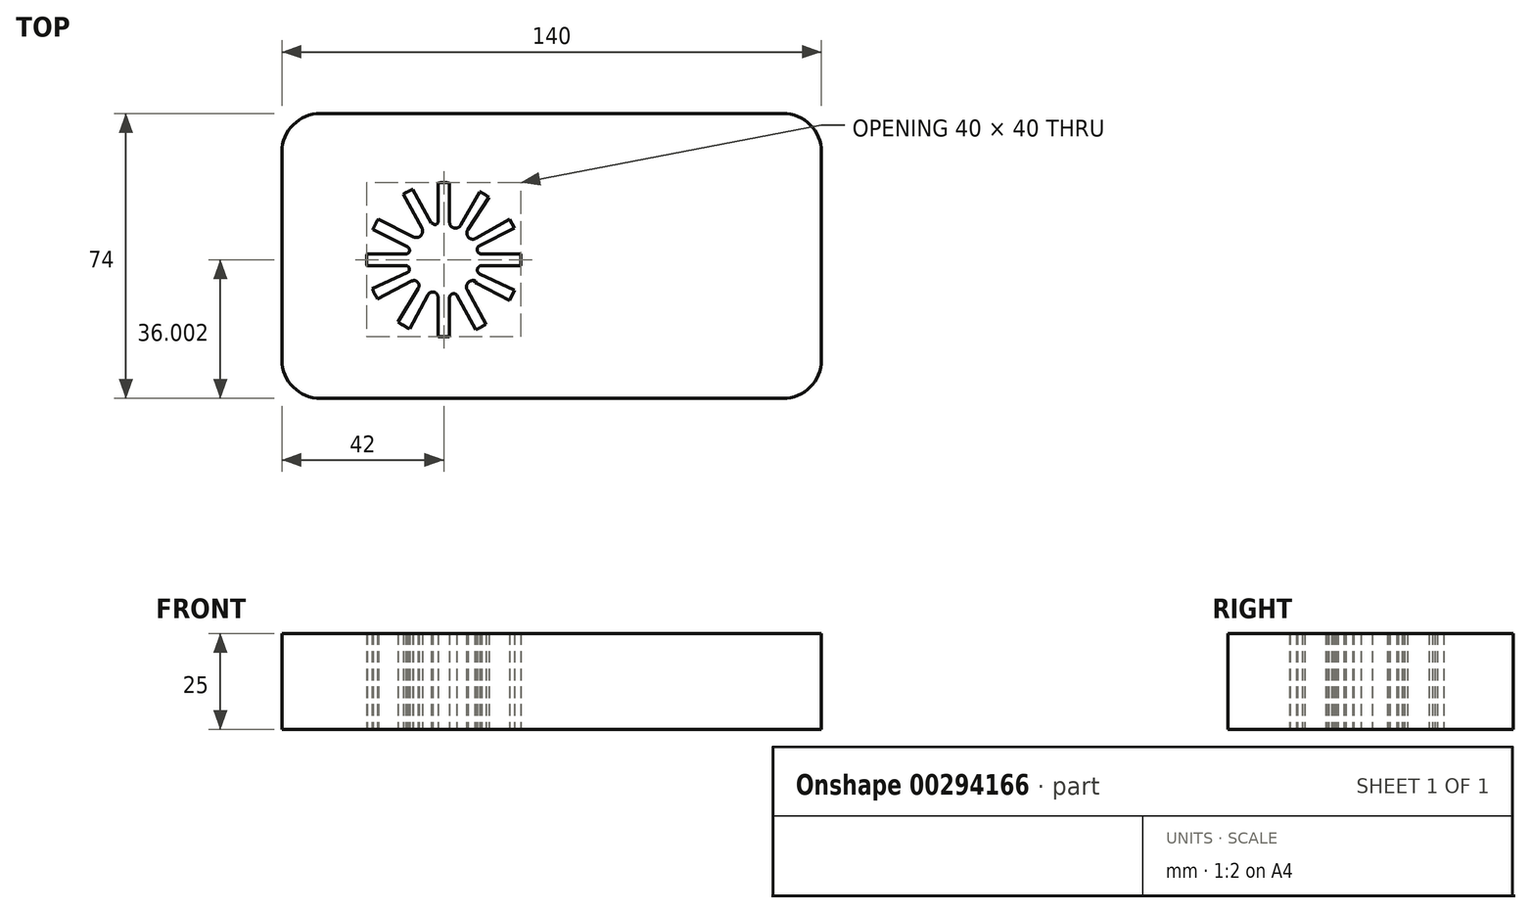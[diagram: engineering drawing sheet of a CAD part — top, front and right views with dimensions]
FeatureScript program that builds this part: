
annotation { "Feature Type Name" : "Feature", "Feature Type Description" : "" }
export const myFeature = defineFeature(function(context is Context, id is Id, definition is map)
    precondition{}
    {
        {
            var Q0;
            Q0=qCreatedBy(makeId("Top.planeOp"),FACE);
            var sketch = newSketch(context, id + "F0", { "sketchPlane" : qUnion([Q0])});
            skArc(sketch, "E0", {"start": v(-58.42, 28.76) * mm, "mid": v(-58.53, 27.26) * mm, "end": v(-58.42, 25.76) * mm});
            skLineSegment(sketch, "E1", {"start": v(-68.47, 28.76) * mm, "end": v(-58.42, 28.76) * mm});
            skLineSegment(sketch, "E2", {"start": v(-68.47, 25.76) * mm, "end": v(-58.42, 25.76) * mm});
            skLineSegment(sketch, "E3", {"start": v(-50.03, 17.38) * mm, "end": v(-50.03, 7.32) * mm});
            skLineSegment(sketch, "E4", {"start": v(-50.03, 7.32) * mm, "end": v(-50.03, 17.38) * mm});
            skLineSegment(sketch, "E5", {"start": v(-47.03, 17.38) * mm, "end": v(-47.03, 7.32) * mm});
            skLineSegment(sketch, "E6", {"start": v(-38.64, 25.76) * mm, "end": v(-28.59, 25.76) * mm});
            skLineSegment(sketch, "E7", {"start": v(-28.59, 25.76) * mm, "end": v(-28.59, 28.76) * mm});
            skLineSegment(sketch, "E8", {"start": v(-28.59, 28.76) * mm, "end": v(-38.64, 28.76) * mm});
            skLineSegment(sketch, "E9", {"start": v(-47.03, 37.15) * mm, "end": v(-47.03, 47.2) * mm});
            skLineSegment(sketch, "E10", {"start": v(-50.03, 47.2) * mm, "end": v(-50.03, 37.15) * mm});
            skLineSegment(sketch, "E11.trimOffspring", {"start": v(-48.96, 27.63) * mm, "end": v(-48.53, 27.26) * mm});
            skLineSegment(sketch, "E12.trimOffspring", {"start": v(-48.53, 27.98) * mm, "end": v(-48.94, 27.61) * mm});
            skLineSegment(sketch, "E13.trimOffspring", {"start": v(-28.59, 27.63) * mm, "end": v(-28.53, 27.63) * mm});
            skLineSegment(sketch, "E14.trimOffspring", {"start": v(-48.96, 27.63) * mm, "end": v(-48.53, 27.63) * mm});
            skLineSegment(sketch, "E15.trimOffspring", {"start": v(-48.53, 27.26) * mm, "end": v(-48.53, 27.98) * mm});
            skPoint(sketch, "E16.start.orphan", {"position": v(-63.67, 40.33) * mm});
            skPoint(sketch, "E17.end.orphan", {"position": v(-63.11, 40.95) * mm});
            skPoint(sketch, "E18.start.orphan", {"position": v(-40.2, 21.72) * mm});
            skPoint(sketch, "E19.trimOffspring.end.orphan", {"position": v(-33.39, 14.2) * mm});
            skPoint(sketch, "E20.end.orphan", {"position": v(-56.85, 21.72) * mm});
            skPoint(sketch, "E21.trimOffspring.end.orphan", {"position": v(-63.67, 14.2) * mm});
            skLineSegment(sketch, "E22", {"start": v(-53.12, 36.25) * mm, "end": v(-53.08, 36.17) * mm});
            skLineSegment(sketch, "E23", {"start": v(-38.44, 44.53) * mm, "end": v(-38.46, 44.5) * mm});
            skLineSegment(sketch, "E24", {"start": v(-52.65, 18.15) * mm, "end": v(-57.35, 9.31) * mm});
            skLineSegment(sketch, "E25", {"start": v(-55.2, 19.8) * mm, "end": v(-60.4, 11.16) * mm});
            skLineSegment(sketch, "E26", {"start": v(-60.4, 11.16) * mm, "end": v(-55.2, 19.8) * mm});
            skLineSegment(sketch, "E27", {"start": v(-56.85, 21.72) * mm, "end": v(-65.77, 17.13) * mm});
            skLineSegment(sketch, "E28", {"start": v(-67.09, 19.8) * mm, "end": v(-57.95, 23.92) * mm});
            skLineSegment(sketch, "E29", {"start": v(-65.77, 37.4) * mm, "end": v(-66.03, 36.94) * mm});
            skLineSegment(sketch, "E30", {"start": v(-65.53, 37.8) * mm, "end": v(-56.54, 33.25) * mm});
            skLineSegment(sketch, "E31", {"start": v(-57.95, 30.6) * mm, "end": v(-66.92, 35.13) * mm});
            skLineSegment(sketch, "E32", {"start": v(-59.05, 44.27) * mm, "end": v(-54.22, 35.49) * mm});
            skLineSegment(sketch, "E33", {"start": v(-54.22, 35.49) * mm, "end": v(-53.12, 36.25) * mm});
            skPoint(sketch, "E34.orphan", {"position": v(-51.46, 37.4) * mm});
            skLineSegment(sketch, "E35", {"start": v(-56.65, 45.54) * mm, "end": v(-51.46, 36.25) * mm});
            skLineSegment(sketch, "E36", {"start": v(-44.14, 36.25) * mm, "end": v(-39.17, 44.94) * mm});
            skLineSegment(sketch, "E37", {"start": v(-39.17, 44.94) * mm, "end": v(-36.85, 43.5) * mm});
            skLineSegment(sketch, "E38", {"start": v(-36.85, 43.5) * mm, "end": v(-42.28, 35.07) * mm});
            skLineSegment(sketch, "E39", {"start": v(-39.24, 23.57) * mm, "end": v(-30.17, 19.34) * mm});
            skLineSegment(sketch, "E40", {"start": v(-31.44, 16.65) * mm, "end": v(-40.2, 21.31) * mm});
            skLineSegment(sketch, "E41", {"start": v(-42.43, 19.34) * mm, "end": v(-37.58, 10.53) * mm});
            skLineSegment(sketch, "E42", {"start": v(-40.2, 9.08) * mm, "end": v(-45.2, 18.15) * mm});
            skArc(sketch, "E43.trimOffspring", {"start": v(-65.53, 37.8) * mm, "mid": v(-66.28, 36.49) * mm, "end": v(-66.92, 35.13) * mm});
            skArc(sketch, "E44.trimOffspring", {"start": v(-56.65, 45.54) * mm, "mid": v(-57.87, 44.95) * mm, "end": v(-59.05, 44.27) * mm});
            skPoint(sketch, "E45.trimOffspring.end.orphan", {"position": v(-48.53, 47.26) * mm});
            skArc(sketch, "E46.trimOffspring", {"start": v(-47.03, 47.2) * mm, "mid": v(-48.53, 47.26) * mm, "end": v(-50.03, 47.2) * mm});
            skArc(sketch, "E47.trimOffspring", {"start": v(-36.85, 43.5) * mm, "mid": v(-37.99, 44.26) * mm, "end": v(-39.17, 44.94) * mm});
            skLineSegment(sketch, "E48.trimOffspring", {"start": v(-48.48, 27.82) * mm, "end": v(-48.95, 27.05) * mm});
            skLineSegment(sketch, "E49.trimOffspring", {"start": v(-48.56, 27.95) * mm, "end": v(-48.26, 27.4) * mm});
            skLineSegment(sketch, "E50.trimOffspring", {"start": v(-48.78, 27.76) * mm, "end": v(-48.18, 27.44) * mm});
            skLineSegment(sketch, "E51.trimOffspring", {"start": v(-48.95, 27.05) * mm, "end": v(-48.18, 27.44) * mm});
            skPoint(sketch, "E52.trimOffspring.end.orphan", {"position": v(-30.73, 36.37) * mm});
            skPoint(sketch, "E53.trimOffspring.end.orphan", {"position": v(-30.73, 18.15) * mm});
            skPoint(sketch, "E54.trimOffspring.end.orphan", {"position": v(-59.05, 10.25) * mm});
            skPoint(sketch, "E55.start.orphan", {"position": v(-66.33, 18.15) * mm});
            skArc(sketch, "E56.trimOffspring", {"start": v(-68.47, 28.76) * mm, "mid": v(-68.53, 27.26) * mm, "end": v(-68.47, 25.76) * mm});
            skArc(sketch, "E57.trimOffspring", {"start": v(-67.09, 19.8) * mm, "mid": v(-66.48, 18.45) * mm, "end": v(-65.77, 17.13) * mm});
            skArc(sketch, "E58.trimOffspring", {"start": v(-60.4, 11.16) * mm, "mid": v(-58.92, 10.17) * mm, "end": v(-57.35, 9.31) * mm});
            skArc(sketch, "E59.trimOffspring", {"start": v(-50.03, 7.32) * mm, "mid": v(-48.53, 7.26) * mm, "end": v(-47.03, 7.32) * mm});
            skArc(sketch, "E60.trimOffspring", {"start": v(-40.2, 9.08) * mm, "mid": v(-38.87, 9.75) * mm, "end": v(-37.58, 10.53) * mm});
            skArc(sketch, "E61.trimOffspring", {"start": v(-28.59, 25.76) * mm, "mid": v(-28.53, 27.26) * mm, "end": v(-28.59, 28.76) * mm});
            skPoint(sketch, "E62.start.orphan", {"position": v(-30.73, 35.49) * mm});
            skLineSegment(sketch, "E63", {"start": v(-31.06, 37) * mm, "end": v(-30.19, 35.49) * mm});
            skLineSegment(sketch, "E64", {"start": v(-30.17, 19.34) * mm, "end": v(-31.44, 16.65) * mm});
            skLineSegment(sketch, "E65", {"start": v(-40.5, 21.31) * mm, "end": v(-40.2, 21.31) * mm});
            skLineSegment(sketch, "E66", {"start": v(-31.44, 37.8) * mm, "end": v(-40.2, 32.8) * mm});
            skLineSegment(sketch, "E67", {"start": v(-39.24, 30.95) * mm, "end": v(-30.19, 35.49) * mm});
            skLineSegment(sketch, "E68", {"start": v(-31.44, 37.8) * mm, "end": v(-30.19, 35.49) * mm});
            skArc(sketch, "E69", {"start": v(-42.28, 35.07) * mm, "mid": v(-42.15, 33.1) * mm, "end": v(-40.2, 32.8) * mm});
            skArc(sketch, "E70", {"start": v(-39.24, 30.95) * mm, "mid": v(-39.83, 29.61) * mm, "end": v(-38.64, 28.76) * mm});
            skArc(sketch, "E71", {"start": v(-38.64, 25.76) * mm, "mid": v(-39.78, 24.9) * mm, "end": v(-39.24, 23.57) * mm});
            skArc(sketch, "E72", {"start": v(-40.2, 21.72) * mm, "mid": v(-42.18, 21.33) * mm, "end": v(-42.43, 19.34) * mm});
            skArc(sketch, "E73", {"start": v(-45.2, 18.15) * mm, "mid": v(-46.37, 18.37) * mm, "end": v(-47.03, 17.38) * mm});
            skArc(sketch, "E74", {"start": v(-50.03, 17.38) * mm, "mid": v(-51.02, 18.83) * mm, "end": v(-52.65, 18.15) * mm});
            skArc(sketch, "E75", {"start": v(-55.2, 19.8) * mm, "mid": v(-55.27, 21.41) * mm, "end": v(-56.85, 21.72) * mm});
            skArc(sketch, "E76", {"start": v(-57.95, 23.92) * mm, "mid": v(-57.47, 25.02) * mm, "end": v(-58.42, 25.76) * mm});
            skArc(sketch, "E77", {"start": v(-58.42, 28.76) * mm, "mid": v(-57.45, 29.5) * mm, "end": v(-57.95, 30.6) * mm});
            skPoint(sketch, "E78.start.orphan", {"position": v(-51.46, 36.82) * mm});
            skArc(sketch, "E79.trimOffspring", {"start": v(-57.95, 23.92) * mm, "mid": v(-57.47, 22.78) * mm, "end": v(-56.85, 21.72) * mm});
            skArc(sketch, "E80.trimOffspring", {"start": v(-55.2, 19.8) * mm, "mid": v(-53.99, 18.88) * mm, "end": v(-52.65, 18.15) * mm});
            skArc(sketch, "E81.trimOffspring", {"start": v(-50.03, 17.38) * mm, "mid": v(-48.53, 17.26) * mm, "end": v(-47.03, 17.38) * mm});
            skArc(sketch, "E82.trimOffspring", {"start": v(-45.05, 17.89) * mm, "mid": v(-43.68, 18.51) * mm, "end": v(-42.43, 19.34) * mm});
            skArc(sketch, "E83.trimOffspring", {"start": v(-40.5, 21.31) * mm, "mid": v(-39.8, 22.4) * mm, "end": v(-39.24, 23.57) * mm});
            skArc(sketch, "E84.trimOffspring", {"start": v(-38.64, 25.76) * mm, "mid": v(-38.53, 27.26) * mm, "end": v(-38.64, 28.76) * mm});
            skArc(sketch, "E85.trimOffspring", {"start": v(-39.24, 30.95) * mm, "mid": v(-39.67, 31.9) * mm, "end": v(-40.2, 32.8) * mm});
            skArc(sketch, "E86.trimOffspring", {"start": v(-42.28, 35.07) * mm, "mid": v(-43.18, 35.7) * mm, "end": v(-44.14, 36.25) * mm});
            skArc(sketch, "E87", {"start": v(-56.54, 33.25) * mm, "mid": v(-54.52, 33.48) * mm, "end": v(-54.22, 35.49) * mm});
            skArc(sketch, "E88", {"start": v(-51.46, 36.82) * mm, "mid": v(-50.62, 36.41) * mm, "end": v(-50.03, 37.15) * mm});
            skArc(sketch, "E89", {"start": v(-47.03, 37.15) * mm, "mid": v(-45.95, 35.54) * mm, "end": v(-44.14, 36.25) * mm});
            skArc(sketch, "E90.trimOffspring", {"start": v(-56.54, 33.25) * mm, "mid": v(-57.34, 31.98) * mm, "end": v(-57.95, 30.6) * mm});
            skArc(sketch, "E91.trimOffspring", {"start": v(-51.46, 36.82) * mm, "mid": v(-52.9, 36.26) * mm, "end": v(-54.22, 35.49) * mm});
            skArc(sketch, "E92.trimOffspring", {"start": v(-47.03, 37.15) * mm, "mid": v(-48.53, 37.26) * mm, "end": v(-50.03, 37.15) * mm});
            skLineSegment(sketch, "E93.bottom", {"start": v(-80.53, 65.26) * mm, "end": v(39.47, 65.26) * mm});
            skLineSegment(sketch, "E93.top", {"start": v(-80.53, -8.74) * mm, "end": v(39.47, -8.74) * mm});
            skLineSegment(sketch, "E93.left", {"start": v(-90.53, 55.26) * mm, "end": v(-90.53, 1.26) * mm});
            skLineSegment(sketch, "E93.right", {"start": v(49.47, 55.26) * mm, "end": v(49.47, 1.26) * mm});
            skPoint(sketch, "E94.visualSharp", {"position": v(-90.53, 65.26) * mm});
            skArc(sketch, "E94.filletArc", {"start": v(-80.53, 65.26) * mm, "mid": v(-87.6, 62.33) * mm, "end": v(-90.53, 55.26) * mm});
            skPoint(sketch, "E95.visualSharp", {"position": v(49.47, 65.26) * mm});
            skArc(sketch, "E95.filletArc", {"start": v(49.47, 55.26) * mm, "mid": v(46.54, 62.33) * mm, "end": v(39.47, 65.26) * mm});
            skPoint(sketch, "E96.visualSharp", {"position": v(49.47, -8.74) * mm});
            skArc(sketch, "E96.filletArc", {"start": v(39.47, -8.74) * mm, "mid": v(46.54, -5.8) * mm, "end": v(49.47, 1.26) * mm});
            skPoint(sketch, "E97.visualSharp", {"position": v(-90.53, -8.74) * mm});
            skArc(sketch, "E97.filletArc", {"start": v(-90.53, 1.26) * mm, "mid": v(-87.6, -5.8) * mm, "end": v(-80.53, -8.74) * mm});
            skSolve(sketch);
        }
        {
            var Q0;
            Q0 = qSketchRegion(id + "F0", true);
            extrude(context, id + "F1", {"entities" : qUnion([Q0]), "depth" : 25 * mm});
        }
    });
